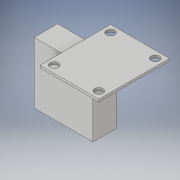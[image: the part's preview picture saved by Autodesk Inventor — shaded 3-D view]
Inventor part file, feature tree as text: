
AUTODESK INVENTOR PART (.ipt)
format: ipt  version: 2019 (Build 230136000, 136)  size: 121,344 bytes
history: native  units: in
note: dims shown in document units (in); Inventor stores cm internally (conversion verified against a paired STEP export)
features: extrude x3, sketch x3
ambient origin geometry x8: Origin, YZ Plane, XZ Plane, XY Plane, X Axis, Y Axis, Z Axis, Center Point
bodies: Solid1 (feature_tree)
feature tree (6):
  extrude  "Extrusion1"  Depth=1.25in
  extrude  "Extrusion2"  Depth=0.05in
  extrude  "Extrusion3"  Depth=1.25in
  sketch  "Sketch1"  dims[d0=1.5in d1=1.25in]
  sketch  "Sketch2"  dims[d2=0.05in d3=0.0in d4=0.15in]
  sketch  "Sketch3"  dims[d5=0.15in d6=0.175in d7=0.05in d8=0.0in d9=0.5in d12=1.3in d13=0.0in d14=0.625in d15=1.25in]
